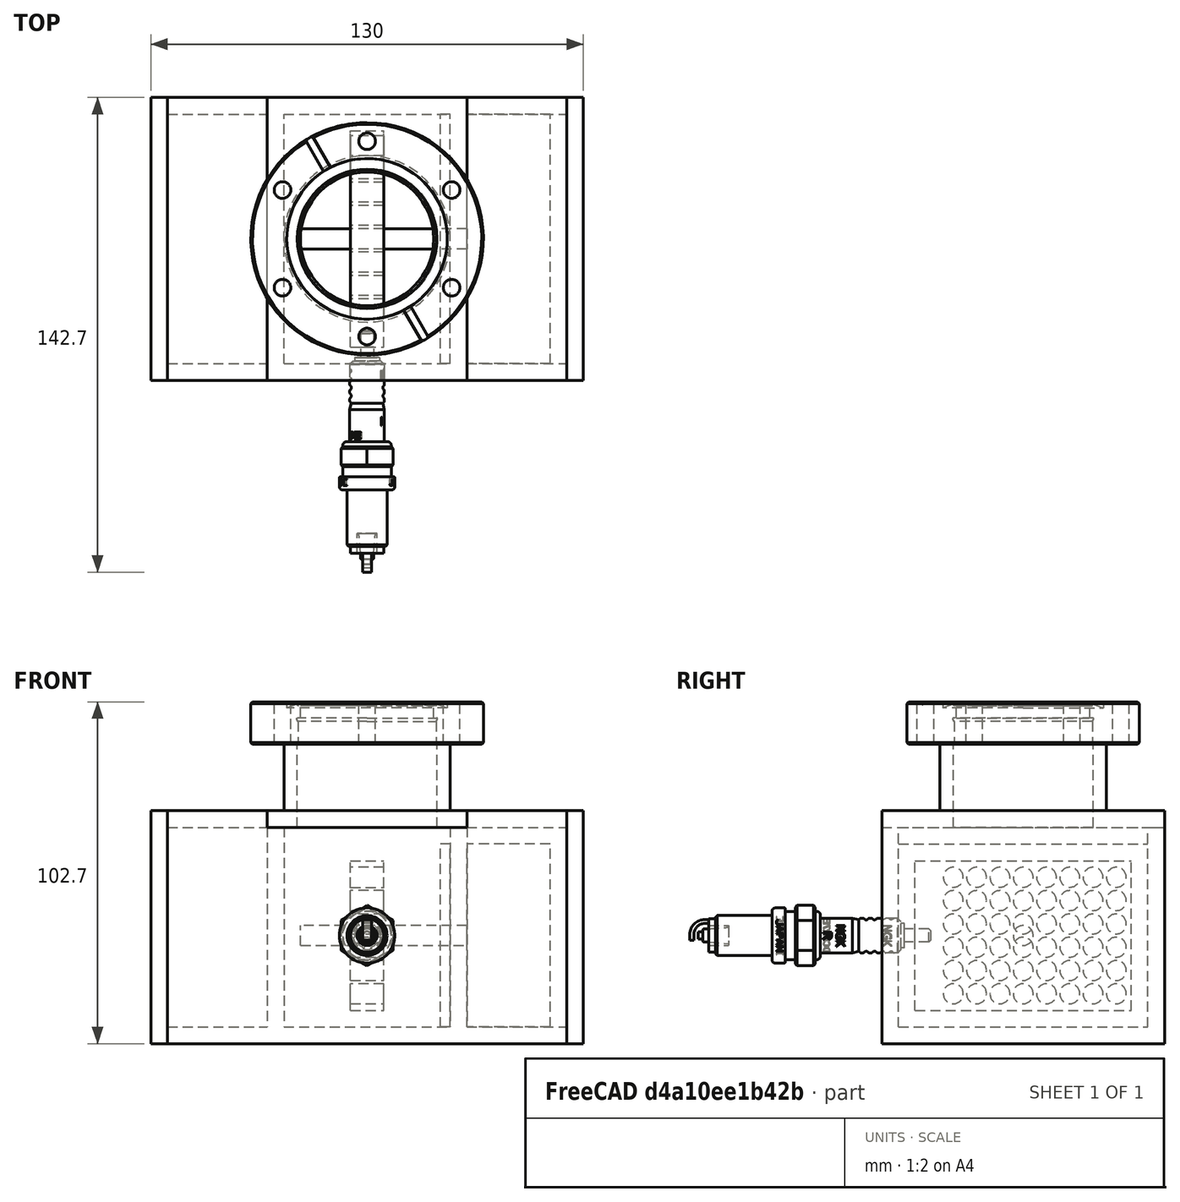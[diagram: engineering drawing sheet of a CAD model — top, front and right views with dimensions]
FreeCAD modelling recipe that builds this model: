
FCSTD DOCUMENT  (FreeCAD 1.0R39285 (Git))
Label: IonPump
License: All rights reserved
LicenseURL: https://en.wikipedia.org/wiki/All_rights_reserved
objects: Part::Box×13, Part::Feature×4, Part::Cut×4, Part::FeaturePython×4, Part::MultiFuse×3, Part::Mirroring×2, Part::Cylinder×1
note: 30 computed .brp shape members not serialized (recipe doc carries the construction recipe); baked Part::Feature solids carry a one-line shape summary decoded from their .brp

FEATURE [Part::Box] Box  label="NeodymiumMagnet"
  AttacherType = Attacher::AttachEngine3D
  Height = 55
  Length = 25
  Placement = pos=(-55,0,0) rot=(0,0,1;0rad)
  Width = 75
FEATURE [Part::Box] Box001  label="TiCathode"
  AttacherType = Attacher::AttachEngine3D
  Height = 55
  Length = 3
  Placement = pos=(-25,0,0) rot=(0,0,1;0rad)
  Width = 75
FEATURE [Part::Feature] Part__Feature009  label="SparkPlug1"
  Placement = pos=(0,-38,27.5) rot=(0,0,1;4.71239rad)
  shape: bbox 163.5 x 72.51 x 18.14 mm, 412 faces (baked)
FEATURE [Part::Mirroring] Part__Mirroring  label="TiCathode (Mirror #1)"
  Base = (0,0,0)
  Normal = (1,0,0)
  Source = -> Box001
FEATURE [Part::Mirroring] Part__Mirroring001  label="NeodymiumMagnet (Mirror #2)"
  Base = (0,0,0)
  Normal = (1,0,0)
  Source = -> Box
FEATURE [Part::Box] Box002  label="Cube"
  AttacherType = Attacher::AttachEngine3D
  Height = 45
  Length = 10
  Placement = pos=(-5,5,5) rot=(0,0,1;0rad)
  Width = 65
FEATURE [Part::Feature] Part__Feature010  label="SparkPlug002"
  Placement = pos=(0,-38,27.5) rot=(0,0,1;4.71239rad)
  shape: bbox 163.5 x 72.51 x 18.14 mm, 412 faces (baked)
FEATURE [Part::Cut] Cut
  Base = -> Box002
  Tool = -> Part__Feature010
FEATURE [Part::Cylinder] Cylinder
  Angle = 360
  AttacherType = Attacher::AttachEngine3D
  FirstAngle = 0
  Height = 50
  Placement = pos=(-20,37.5,27.5) rot=(0,1,0;1.5708rad)
  Radius = 3
  SecondAngle = 0
FEATURE [Part::FeaturePython] Array  # Draft array (typed FeaturePython)
  AlwaysSyncPlacement = false
  Angle = 360
  ArrayType = 0
  Axis = (0,0,1)
  Base = -> Cylinder
  Center = (0,0,0)
  Count = 48
  ExpandArray = false
  Fuse = false
  IntervalAxis = (0,0,0)
  IntervalX = (100,0,0)
  IntervalY = (0,7,0)
  IntervalZ = (0,0,7)
  NumberCircles = 3
  NumberPolar = 5
  NumberX = 1
  NumberY = 8
  NumberZ = 6
  Placement = pos=(0,-21,-17.5) rot=(0,0,1;0rad)
  PlacementList = 48 placements: [(-20,37.5,27.5),(-20,37.5,34.5),(-20,37.5,41.5),(-20,37.5,48.5),(-20,37.5,55.5),(-20,37.5,62.5),(-20,44.5,27.5),(-20,44.5,34.5),(-20,44.5,41.5),(-20,44.5,48.5),(-20,44.5,55.5),(-20,44.5,62.5),(-20,51.5,27.5),(-20,51.5,34.5),(-20,51.5,41.5),(-20,51.5,48.5),(-20,51.5,55.5),(-20,51.5,62.5),(-20,58.5,27.5),(-20,58.5,34.5),(-20,58.5,41.5),(-20,58.5,48.5),(-20,58.5,55.5),(-20,58.5,62.5),(-20,65.5,27.5),+23 more]
  RadialDistance = 50
  ScaleList = (48) [(1,1,1),(1,1,1),(1,1,1),(1,1,1),(1,1,1),(1,1,1),(1,1,1),(1,1,1),(1,1,1),(1,1,1),(1,1,1),(1,1,1),(1,1,1),(1,1,1),(1,1,1),(1,1,1),(1,1,1),(1,1,1),+30 more]
  Symmetry = 1
  TangentialDistance = 25
FEATURE [Part::Cut] Cut001  label="Anode"
  Base = -> Cut
  Tool = -> Array
FEATURE [Part::Box] Box003  label="Cube001"
  AttacherType = Attacher::AttachEngine3D
  Height = 65
  Length = 5
  Placement = pos=(-30,-5,-5) rot=(0,0,1;0rad)
  Width = 85
FEATURE [Part::Box] Box004  label="Cube002"
  AttacherType = Attacher::AttachEngine3D
  Height = 65
  Length = 5
  Placement = pos=(25,-5,-5) rot=(0,0,1;0rad)
  Width = 85
FEATURE [Part::Box] Box005  label="Cube003"
  AttacherType = Attacher::AttachEngine3D
  Height = 5
  Length = 120
  Placement = pos=(-60,-5,-5) rot=(0,0,1;0rad)
  Width = 85
FEATURE [Part::Box] Box006  label="Cube004"
  AttacherType = Attacher::AttachEngine3D
  Height = 65
  Length = 120
  Placement = pos=(-60,-5,-5) rot=(0,0,1;0rad)
  Width = 5
FEATURE [Part::Feature] Part__Feature011  label="SparkPlug003"
  Placement = pos=(0,-24,27.5) rot=(0,0,1;4.71239rad)
  shape: bbox 163.5 x 72.51 x 18.14 mm, 412 faces (baked)
FEATURE [Part::Cut] Cut002
  Base = -> Box006
  Tool = -> Part__Feature011
FEATURE [Part::Box] Box007  label="Cube005"
  AttacherType = Attacher::AttachEngine3D
  Height = 65
  Length = 120
  Placement = pos=(-60,75,-5) rot=(0,0,1;0rad)
  Width = 5
FEATURE [Part::Box] Box008  label="Cube006"
  AttacherType = Attacher::AttachEngine3D
  Height = 5
  Length = 30
  Placement = pos=(-60,-5,60) rot=(0,0,1;0rad)
  Width = 85
FEATURE [Part::Box] Box009  label="Cube007"
  AttacherType = Attacher::AttachEngine3D
  Height = 5
  Length = 30
  Placement = pos=(30,-5,60) rot=(0,0,1;0rad)
  Width = 85
FEATURE [Part::MultiFuse] Fusion  label="Housing"
  Shapes = -> [Box009,Box008,Box007,Cut002,Box005,Box004,Box003]
FEATURE [Part::Box] Box010  label="MagnetCover"
  AttacherType = Attacher::AttachEngine3D
  Height = 70
  Length = 5
  Placement = pos=(60,-5,-5) rot=(0,0,1;0rad)
  Width = 85
FEATURE [Part::Box] Box011  label="MagnetCover2"
  AttacherType = Attacher::AttachEngine3D
  Height = 70
  Length = 5
  Placement = pos=(-65,-5,-5) rot=(0,0,1;0rad)
  Width = 85
FEATURE [Part::Box] Box012  label="Cube008"
  AttacherType = Attacher::AttachEngine3D
  Height = 5
  Length = 60
  Placement = pos=(-30,-5,60) rot=(0,0,1;0rad)
  Width = 85
FEATURE [Part::Feature] Part__Feature  label="wh"
  Placement = pos=(0,0,90) rot=(1,0,0;1.5708rad)
  shape: bbox 69.9 x 69.9 x 12.7 mm, 278 faces (baked)
FEATURE [Part::FeaturePython] Tube  # WARN: FeaturePython — macro-defined, semantics opaque (R4)
  AttacherType = Attacher::AttachEngine3D
  Height = 10.5
  InnerRadius = 32
  OuterRadius = 34.95
  Placement = pos=(0,0,91) rot=(0,0,1;0rad)
FEATURE [Part::MultiFuse] Fusion001  label="gyggi"
  Placement = pos=(0,37.5,-5) rot=(0,0,1;0rad)
  Shapes = -> [Part__Feature,Tube]
FEATURE [Part::FeaturePython] Tube001  # WARN: FeaturePython — macro-defined, semantics opaque (R4)
  AttacherType = Attacher::AttachEngine3D
  Height = 20
  InnerRadius = 21
  OuterRadius = 25
  Placement = pos=(0,37.5,65) rot=(0,0,1;0rad)
FEATURE [Part::FeaturePython] Tube002  # WARN: FeaturePython — macro-defined, semantics opaque (R4)
  AttacherType = Attacher::AttachEngine3D
  Height = 20
  InnerRadius = 0
  OuterRadius = 21
  Placement = pos=(0,37.5,55) rot=(0,0,1;0rad)
FEATURE [Part::Cut] Cut003
  Base = -> Box012
  Tool = -> Tube002
FEATURE [Part::MultiFuse] Fusion002  label="DN35-40"
  Shapes = -> [Cut003,Tube001,Fusion001]
